# Revit family: SQ Series Nozzles
name_source: partatom
category: Conexões de tubo
units: mm (PartAtom-declared; Revit-internal decimal feet)

## family parameters
Com base no plano de trabalho = Sim
Compartilhado = Não
Corte com vazios quando carregada = Não
Cota do conector redondo = Utilizar diâmetro
Número OmniClass = 23.60.30.11.14
Sempre na vertical = Sim
Tipo de parte = Cobertura
Título OmniClass = Pipework Fittings

## types (6) — shared parameters
Blue Plastic = Transparent Plastic
DT1 = 0 ft
DT12 = 0 ft
DT13 = 0 ft
DT2 = 0 ft
DT6 = 0 ft
Elevação-padrão = 4 ft
H2 = 1 ft
Metal = PARAFUSO
Plastic 1 = Plastic Black
Plastic 2 = Black Plastic
RainBird: Product Link = https://store.rainbird.com
Reviw = R00
SupportProjetos: Level of Detail = LOD 300
Type = 5 ft
URL = https://www.rainbird.com
Water = Water

## per-type parameters (varying)
| type | Descrição | RainBird: Description |
| SQ-QTR | SQ-QTR: SQ Nozzle, quarter pattern | SQ-QTR: SQ Nozzle, quarter pattern |
| SQ-HLF | SQ-HLF: SQ Nozzle, half pattern | SQ-HLF: SQ Nozzle, half pattern |
| SQ-FUL | SQ-FUL: SQ Nozzle, full pattern | SQ-FUL: SQ Nozzle, full pattern |
| SQ-ADP12 | SQ-ADP12: SQ Nozzle Adapter with 12" PolyFlex Riser | SQ-ADP12: SQ Nozzle Adapter with 12" PolyFlex Riser |
| SQ-ADP24 | SQ-ADP24: SQ Nozzle Adapter with 24" PolyFlex Riser | SQ-ADP24: SQ Nozzle Adapter with 24" PolyFlex Riser |
| SQ-ADP | SQ-ADP: SQ PolyFlex Riser Adapter only | SQ-ADP: SQ PolyFlex Riser Adapter only |

note: column(s) folded — value = type name in every type: Modelo
